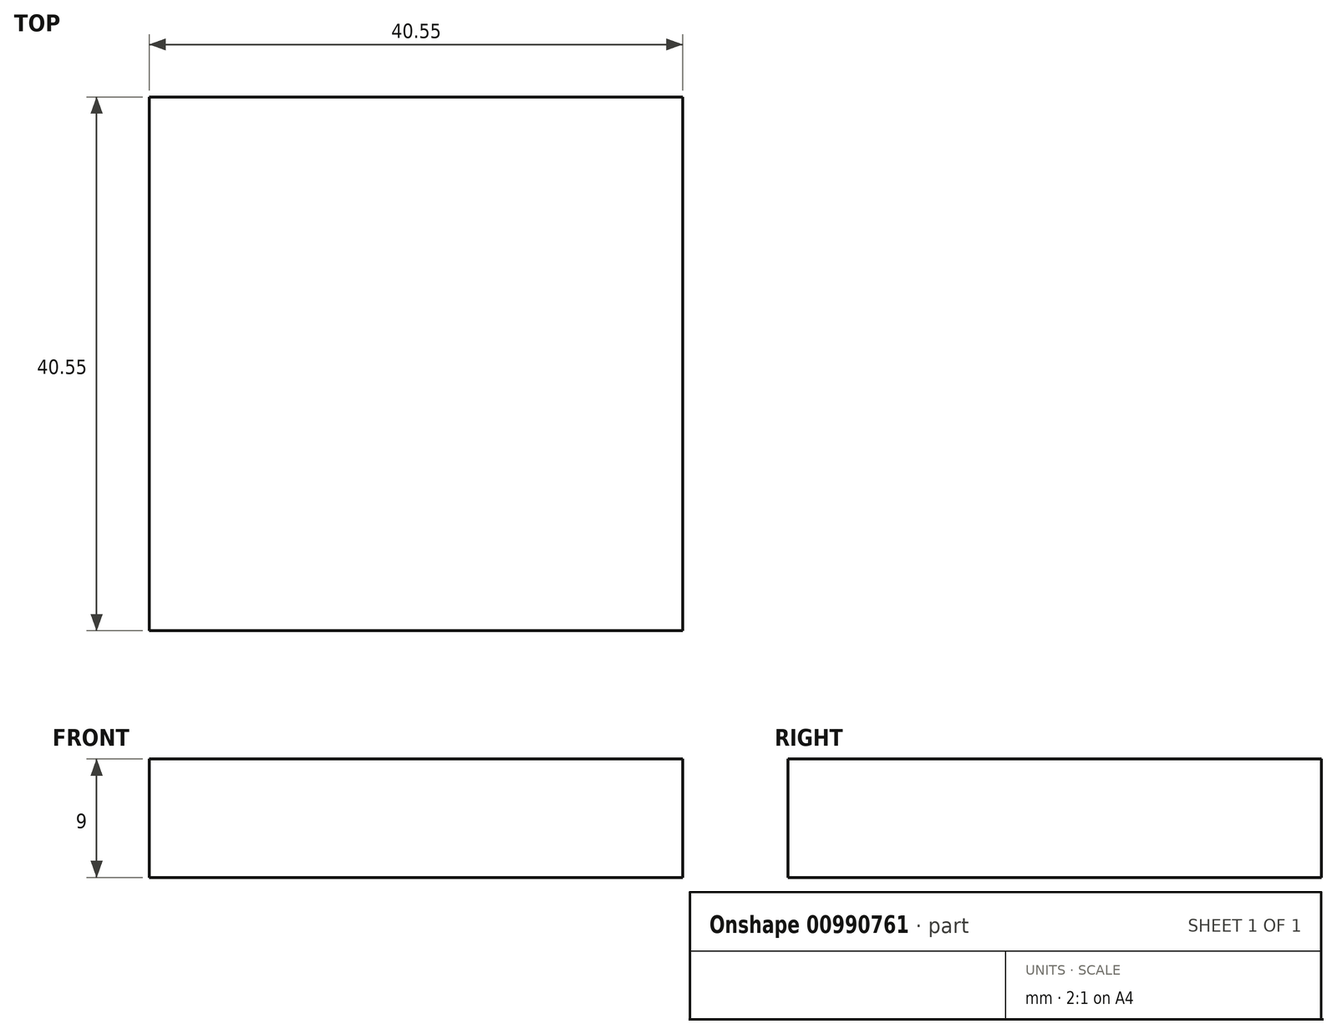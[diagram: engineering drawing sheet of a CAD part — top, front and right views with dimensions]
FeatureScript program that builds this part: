
annotation { "Feature Type Name" : "Feature", "Feature Type Description" : "" }
export const myFeature = defineFeature(function(context is Context, id is Id, definition is map)
    precondition{}
    {
        {
            var Q0;
            Q0=qCreatedBy(makeId("Top.planeOp"),FACE);
            var sketch = newSketch(context, id + "F0", { "sketchPlane" : qUnion([Q0])});
            skLineSegment(sketch, "E0.bottom", {"start": v(-50.45, 44.47) * mm, "end": v(-9.9, 44.47) * mm});
            skLineSegment(sketch, "E0.top", {"start": v(-50.45, 3.92) * mm, "end": v(-9.9, 3.92) * mm});
            skLineSegment(sketch, "E0.left", {"start": v(-50.45, 44.47) * mm, "end": v(-50.45, 3.92) * mm});
            skLineSegment(sketch, "E0.right", {"start": v(-9.9, 44.47) * mm, "end": v(-9.9, 3.92) * mm});
            skSolve(sketch);
        }
        {
            var Q0;
            Q0 = qSketchRegion(id + "F0", true);
            extrude(context, id + "F1", {"entities" : qUnion([Q0]), "depth" : 9 * mm, "offsetDistance" : 25 * mm});
        }
    });
